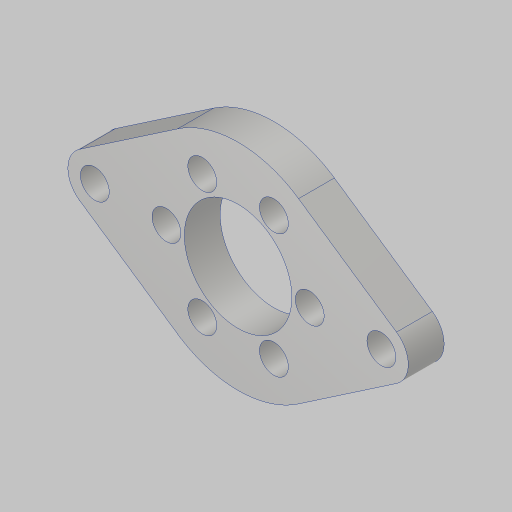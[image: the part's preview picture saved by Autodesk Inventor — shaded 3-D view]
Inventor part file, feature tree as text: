
AUTODESK INVENTOR PART (.ipt)
format: ipt  version: 2023.5 (Build 275446000, 446)  size: 141,312 bytes
history: native  units: in
note: dims shown in document units (in); Inventor stores cm internally (conversion verified against a paired STEP export)
features: sketch x1, extrude x1, hole x1
ambient origin geometry x8: Origin, YZ Plane, XZ Plane, XY Plane, X Axis, Y Axis, Z Axis, Center Point
bodies: Solid1 (feature_tree)
feature tree (3):
  sketch  "Sketch1"  dims[d0=0.375in d1=0.375in d2=2.0in d3=1.5in d4=0.75in d5=1.0in d6=2.3622in d8=360.0deg d11=0.25in d12=0.0in d13=0.201in d14=0.75in d15=0.385in d16=0.25in d17=0.5635in d18=1.0in d19=0.8108in]
  extrude  "Extrusion1"  Depth=0.375in
  hole  "Hole1"  [1 undecoded]
note: 1 required parameter value undecoded (feature->parameter linkage not recoverable at this tier; creation-order binding heuristic only, values carry confidence <= 0.55)
